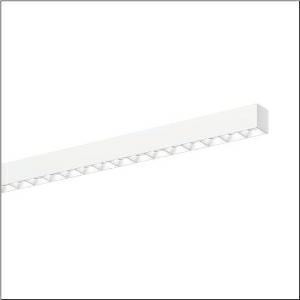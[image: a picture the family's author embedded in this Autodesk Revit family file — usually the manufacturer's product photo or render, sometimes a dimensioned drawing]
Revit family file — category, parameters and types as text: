
# Revit family: silica_r__21_51mx26dc3awb_8cf9
name_source: partatom
category: Lighting Fixtures
units: mm (PartAtom-declared; Revit-internal decimal feet)

## family parameters
Cut with Voids When Loaded = No
Host = Face
Light Source = No
Part Type = Normal
Room Calculation Point = No
Round Connector Dimension = Use Diameter
Shared = No

## types (1)
- --- (1 x LED, 10800 lm, 63.6 W, 3000K)
    Apparent Load = 64 VA
    CIE Flux Codes = 83 98 100 100 100
    Color Rendering = 80
    Color Temperature = 3000K
    Default Elevation = 1800 mm
    Description = Silica® 21, office luminaire, primary light control with darklight reflector, of PMMA, white, CAT 2 (L<= 3000cd/m²), light emission: direct distribution, primary light characteristic: symmetric, installation type: surface-mounted, LED, rated luminous flux: 10.800lm, luminous efficacy: 170lm/W, light colour: 830, colour temperature: 3000K, control gear: DALI 2, with terminal, 3+2-pole, max. 2.5mm², mains connection: 220..240V, AC, 50/60Hz, rated input power: 63.6W, luminaire housing, of aluminium, traffic white (RAL 9016), length: 3.004mm, width: 53mm, height: 53mm, protection rating (complete): IP20, insulation class (complete): insulation class I (protective earthing), certification: CE, permissible operating ambient temperature: 0..+35°C, standard: EN 50419, packaging unit: 1 piece
    Height = 53 mm
    Lamp = 1 x LED
    Lamp Light Flux = 10800 lm
    Lamp Power = 63.6 W
    Lamp count = 1
    Length = 3004 mm
    Luminous efficacy = 170 lm/W
    Manufacturer = Siteco
    ModVariant = No
    Model = 51MX26DC3AWB
    Mounting Place = Ceiling
    Mounting Type = Surface mounted
    Number of Poles = 1
    OnlyDefault = Yes
    Power Factor = 1
    Product Name = Silica® 21
    Product group = office luminaire | ceiling mounted
    ProductGroupID = 302
    Protection Class = Protection class I
    Protection Degree = IP 20
    RLX_Detail_Level = 1
    RLX_Emergency_Light_Flux = 0 lm
    RLX_Emergency_Type = 0
    RLX_Emergency_Type_DB = No
    RlxData = <blob elided: 59985 chars, md5=60685643>
    Socket = socket
    Standby Power = 0 W
    System Light Flux = 10800 lm
    System Power = 64 W
    Type Comments = factory setting: luminous flux: 100 % | dim-lin: 254 | 360 mA
    Type Image = l_1335934.jpg
    URL = http://relux.com
    VarID = @adj_124168
    Voltage = 0 V
    Weight = 0.00 kg
    Width = 53 mm

## geometry (parser evidence)
native form markers: Blend x4, Sweep x12
no freeform markers — native parametric forms only
